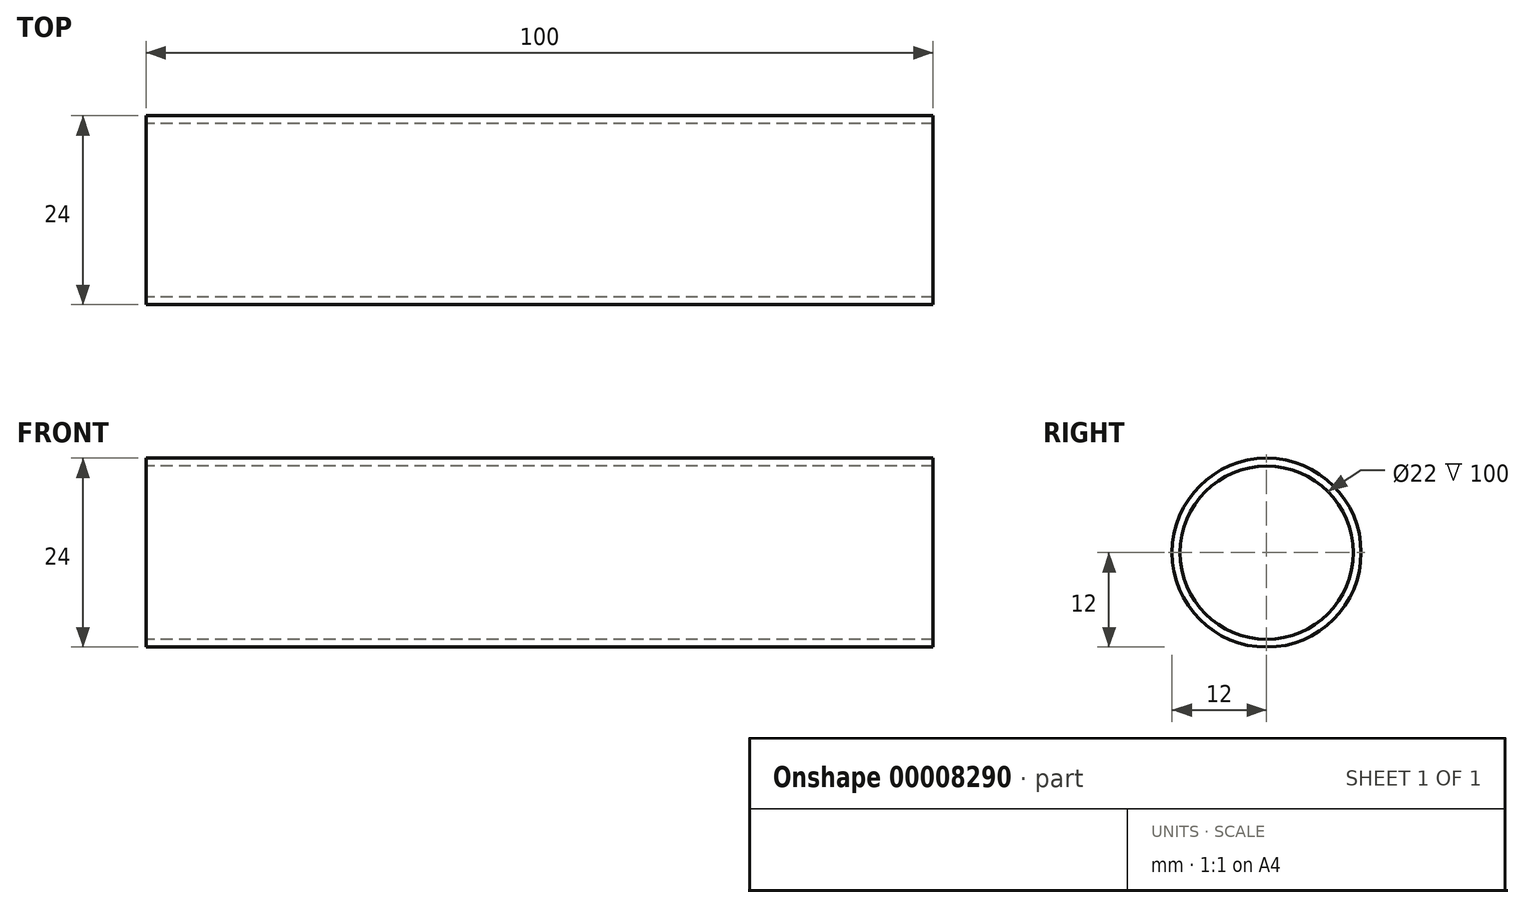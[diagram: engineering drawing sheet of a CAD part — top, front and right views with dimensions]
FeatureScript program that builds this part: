
annotation { "Feature Type Name" : "Feature", "Feature Type Description" : "" }
export const myFeature = defineFeature(function(context is Context, id is Id, definition is map)
    precondition{}
    {
        {
            var Q0;
            Q0=qCreatedBy(makeId("Right.planeOp"),FACE);
            var sketch = newSketch(context, id + "F0", { "sketchPlane" : qUnion([Q0])});
            skCircle(sketch, "E0", {"center": v(0, 0) * mm, "radius": 12 * mm});
            skCircle(sketch, "E1", {"center": v(0, 0) * mm, "radius": 11 * mm});
            skSolve(sketch);
        }
        {
            var Q0;
            Q0=makeQuery(id+"F0.imprint","IMPRINT",FACE,{"disambiguationData":[TD([[makeQuery(id+"F0.imprint","IMPRINT",EDGE,{"derivedFrom":sQuery(id+"F0.wireOp",EDGE,"E0")}),1.0]])]});
            extrude(context, id + "F1", {"entities" : qUnion([Q0]), "depth" : 100 * mm});
        }
    });
